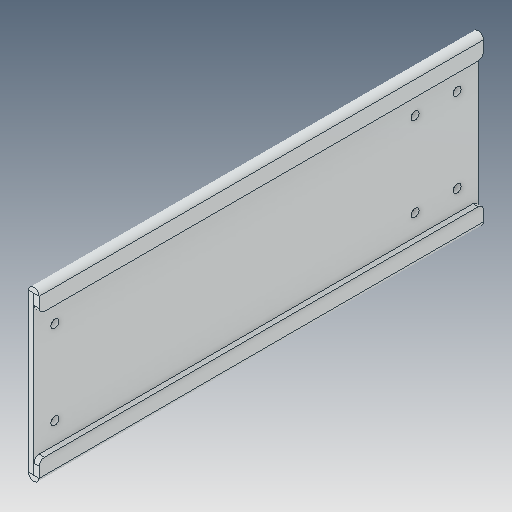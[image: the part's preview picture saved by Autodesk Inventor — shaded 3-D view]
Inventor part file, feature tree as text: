
AUTODESK INVENTOR PART (.ipt)
format: ipt  version: 2023.5 (Build 275446000, 446)  size: 120,832 bytes
history: native  units: in
note: dims shown in document units (in); Inventor stores cm internally (conversion verified against a paired STEP export)
features: fillet x1
ambient origin geometry x8: Origin, YZ Plane, XZ Plane, XY Plane, X Axis, Y Axis, Z Axis, Center Point
bodies: Solid1 (feature_tree)
feature tree (1):
  fillet  "Fillet1"  [1 undecoded]
note: 1 required parameter value undecoded (feature->parameter linkage not recoverable at this tier; creation-order binding heuristic only, values carry confidence <= 0.55)
